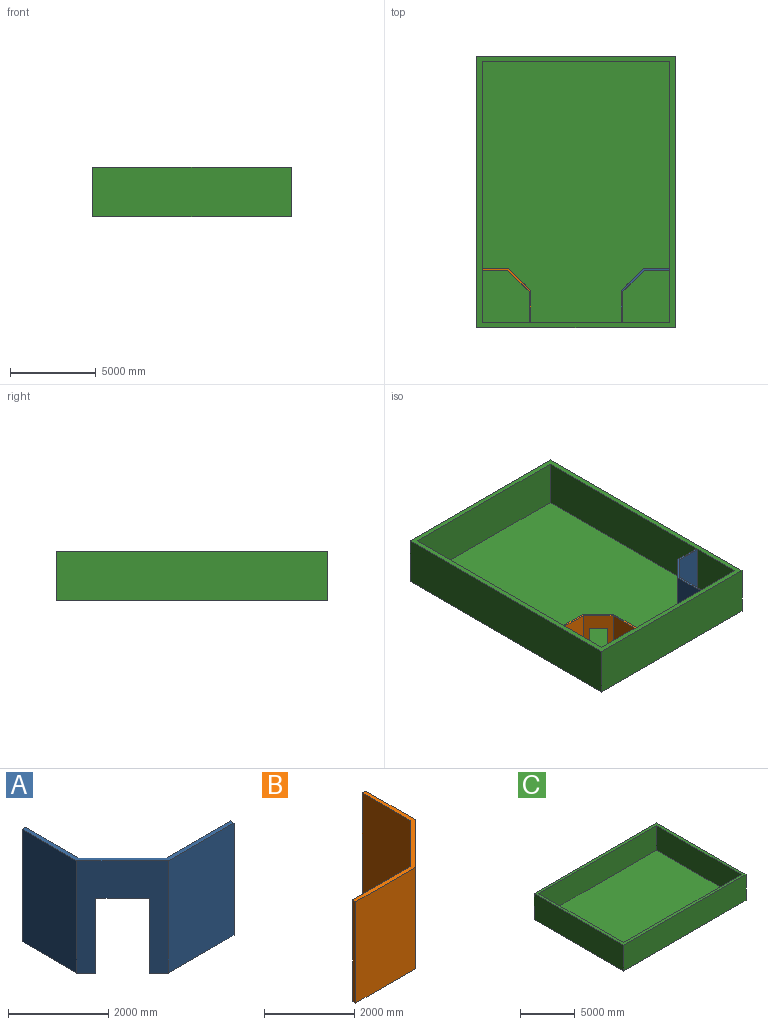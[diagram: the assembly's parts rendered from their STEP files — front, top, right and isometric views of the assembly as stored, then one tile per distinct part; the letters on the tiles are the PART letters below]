
ASSEMBLY  parts=3 mates=6
PART A: 14 faces, bbox 3149.6x2844.8x2743.2 mm
  f0: plane 2743.2x1856.44mm, normal (0,-1,0), area 5092594.8mm2, adj f3,f4,f5,f13
  f1: plane 1821.05x341.25mm, normal (0,0,-1), area 192080.8mm2, adj f2,f3,f6,f8,f9,f12
  f2: plane 2743.2x1551.64mm, normal (-1,0,0), area 4256467.4mm2, adj f1,f3,f4,f12
  f3: plane 2743.2x1293.16mm, normal (-0.71,-0.71,0), area 3065800.3mm2, adj f0,f1,f2,f4,f5,f9,f10,f11
  f4: plane 3149.6x2844.8mm, normal (0,0,1), area 523516.2mm2, adj f0,f2,f3,f6,f7,f8,f12,f13
  f5: plane 2125.85x341.25mm, normal (0,0,-1), area 223048.5mm2, adj f0,f3,f7,f8,f10,f13
  f6: plane 2743.2x1509.56mm, normal (1,0,0), area 4141022.3mm2, adj f1,f4,f8,f12
  f7: plane 2743.2x1814.36mm, normal (0,1,0), area 4977149.7mm2, adj f4,f5,f8,f13
  f8: plane 2743.2x1233.64mm, normal (0.71,0.71,0), area 2834910.1mm2, adj f1,f4,f5,f6,f7,f9,f10,f11
  f9: plane 1828.8x71.84mm, normal (0.71,-0.71,0), area 185806.1mm2, adj f1,f3,f8,f11
  f10: plane 1828.8x71.84mm, normal (-0.71,0.71,0), area 185806.1mm2, adj f3,f5,f8,f11
  f11: plane 826.18x826.18mm, normal (0,0,-1), area 108386.9mm2, adj f3,f8,f9,f10
  f12: plane 2743.2x101.6mm, normal (0,1,0), area 278709.1mm2, adj f1,f2,f4,f6
  f13: plane 2743.2x101.6mm, normal (1,0,0), area 278709.1mm2, adj f0,f4,f5,f7
PART B: 14 faces, bbox 3149.6x2844.8x2743.2 mm
  f0: plane 2743.2x1856.44mm, normal (0,-1,0), area 5092594.8mm2, adj f3,f4,f5,f13
  f1: plane 1821.05x341.25mm, normal (0,0,-1), area 192080.8mm2, adj f2,f3,f6,f8,f9,f12
  f2: plane 2743.2x1551.64mm, normal (1,0,0), area 4256467.4mm2, adj f1,f3,f4,f12
  f3: plane 2743.2x1293.16mm, normal (0.71,-0.71,0), area 3065800.3mm2, adj f0,f1,f2,f4,f5,f9,f10,f11
  f4: plane 3149.6x2844.8mm, normal (0,0,1), area 523516.2mm2, adj f0,f2,f3,f6,f7,f8,f12,f13
  f5: plane 2125.85x341.25mm, normal (0,0,-1), area 223048.5mm2, adj f0,f3,f7,f8,f10,f13
  f6: plane 2743.2x1509.56mm, normal (-1,0,0), area 4141022.3mm2, adj f1,f4,f8,f12
  f7: plane 2743.2x1814.36mm, normal (0,1,0), area 4977149.7mm2, adj f4,f5,f8,f13
  f8: plane 2743.2x1233.64mm, normal (-0.71,0.71,0), area 2834910.1mm2, adj f1,f4,f5,f6,f7,f9,f10,f11
  f9: plane 1828.8x71.84mm, normal (-0.71,-0.71,0), area 185806.1mm2, adj f1,f3,f8,f11
  f10: plane 1828.8x71.84mm, normal (0.71,0.71,0), area 185806.1mm2, adj f3,f5,f8,f11
  f11: plane 826.18x826.18mm, normal (0,0,-1), area 108386.9mm2, adj f3,f8,f9,f10
  f12: plane 2743.2x101.6mm, normal (0,1,0), area 278709.1mm2, adj f1,f2,f4,f6
  f13: plane 2743.2x101.6mm, normal (-1,0,0), area 278709.1mm2, adj f0,f4,f5,f7
PART C: 11 faces, bbox 15849.6x11582.4x2895.6 mm
  f0: plane 10972.8x2743.2mm, normal (1,0,0), area 30100585mm2, adj f1,f7,f8,f9
  f1: plane 15240x2743.2mm, normal (0,-1,0), area 41806368mm2, adj f0,f2,f8,f9
  f2: plane 10972.8x2743.2mm, normal (-1,0,0), area 30100585mm2, adj f1,f7,f8,f9
  f3: plane 11582.4x2895.6mm, normal (1,0,0), area 33537997.4mm2, adj f4,f6,f8,f10
  f4: plane 15849.6x2895.6mm, normal (0,1,0), area 45894101.8mm2, adj f3,f5,f8,f10
  f5: plane 11582.4x2895.6mm, normal (-1,0,0), area 33537997.4mm2, adj f4,f6,f8,f10
  f6: plane 15849.6x2895.6mm, normal (0,-1,0), area 45894101.8mm2, adj f3,f5,f8,f10
  f7: plane 15240x2743.2mm, normal (0,1,0), area 41806368mm2, adj f0,f2,f8,f9
  f8: plane 15849.6x11582.4mm, normal (0,0,1), area 16350935mm2, adj f0,f1,f2,f3,f4,f5,f6,f7
  f9: plane 15240x10972.8mm, normal (0,0,1), area 167225472mm2, adj f0,f1,f2,f7
  f10: plane 15849.6x11582.4mm, normal (0,0,-1), area 183576407mm2, adj f3,f4,f5,f6
PLACE A rot(axis=(0,0,-1),90deg) t=(5588,-7721.6,0)mm
PLACE B rot(axis=(0,0,1),90deg) t=(-5588,-7721.6,0)mm
PLACE C rot(axis=(0,0,1),90deg) t=(0,0,0)mm
MATE planar B.f12 <-> C.f1  axis (-1,0,0) through (-5486.4,-4572,1371.6)mm
MATE planar A.f13 <-> C.f0  axis (0,-1,0) through (2692.4,-7620,1371.6)mm
MATE planar C.f7 <-> A.f12  axis (-1,0,0) through (5486.4,0,1371.6)mm
MATE planar C.f9 <-> B.f5  axis (0,0,1) through (0,0,0)mm
MATE planar C.f9 <-> A.f1  axis (0,0,1) through (0,0,0)mm
MATE planar C.f0 <-> B.f13  axis (0,1,0) through (0,-7620,1371.6)mm
